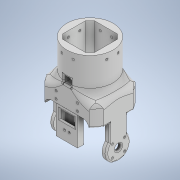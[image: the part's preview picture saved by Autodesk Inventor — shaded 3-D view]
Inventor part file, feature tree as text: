
AUTODESK INVENTOR PART (.ipt)
format: ipt  version: 2021 (Build 250183000, 183)  size: 1,526,272 bytes
history: native  units: mm
features: sketch x24, extrude x23, fillet x15, other x1
ambient origin geometry x8: Origin, YZ Plane, XZ Plane, XY Plane, X Axis, Y Axis, Z Axis, Center Point
bodies: Body1 (feature_tree)
feature tree (63):
  other  "Sólido1"
  extrude  "Extrusión1"  Depth=40.0mm
  extrude  "Extrusión2"  Depth=2.0mm
  fillet  "Empalme1"  Radius=400.0mm
  extrude  "Extrusión3"  Depth=40.0mm TaperAngle=0.0deg
  extrude  "Extrusión4"  Depth=12.0mm TaperAngle=0.0deg
  extrude  "Extrusión5"  Depth=9.0mm TaperAngle=0.0deg
  extrude  "Extrusión7"  Depth=2.0mm
  extrude  "Extrusión8"  Depth=50.0mm TaperAngle=0.0deg
  extrude  "Extrusión9"  Depth=10.0mm
  fillet  "Empalme2"  Radius=10.0mm
  fillet  "Empalme3"  Radius=10.0mm
  extrude  "Extrusión10"  Depth=10.0mm
  extrude  "Extrusión11"  Depth=10.0mm
  fillet  "Empalme4"  Radius=3.0mm
  fillet  "Empalme5"  Radius=500.0mm
  fillet  "Empalme6"  Radius=3.0mm
  fillet  "Empalme7"  Radius=3.0mm
  fillet  "Empalme8"  Radius=500.0mm
  fillet  "Empalme9"  Radius=3.0mm
  fillet  "Empalme10"  Radius=3.0mm
  extrude  "Extrusión12"  Depth=3.0mm
  extrude  "Extrusión13"  Depth=5.0mm
  extrude  "Extrusión14"  Depth=10.0mm
  extrude  "Extrusión15"  Depth=2.0mm
  fillet  "Empalme11"  Radius=0.1mm
  fillet  "Empalme12"  Radius=1.5mm
  extrude  "Extrusión16"  Depth=30.0mm TaperAngle=0.0deg
  extrude  "Extrusión17"  Depth=40.0mm TaperAngle=360.0deg
  extrude  "Extrusión18"  Depth=2.0mm
  fillet  "Empalme14"  Radius=18.0mm
  sketch  "Boceto25"  dims[d130=16.0mm d133=30.0mm d134=40.0mm d135=0.0mm]
  extrude  "Extrusión19"  Depth=30.0mm
  fillet  "Empalme15"  Radius=40.0mm
  extrude  "Extrusión20"  Depth=25.0mm TaperAngle=0.0deg
  extrude  "Extrusión22"  Depth=5.0mm TaperAngle=0.0deg
  extrude  "Extrusión23"  Depth=2.0mm
  extrude  "Extrusión24"  [1 undecoded]
  extrude  "Extrusión25"  [1 undecoded]
  fillet  "Empalme16"  [1 undecoded]
  sketch  "Boceto1"  dims[d7=40.0mm d8=0.0mm d10=8.0mm]
  sketch  "Boceto2"  dims[d11=400.0mm d12=0.0mm d13=2.0mm d16=400.0mm d17=0.0mm]
  sketch  "Boceto3"  dims[d18=400.0mm d19=0.0mm d20=40.0mm d21=0.0mm]
  sketch  "Boceto4"  dims[d25=62.249mm d26=0.0mm d27=12.0mm d28=0.0mm]
  sketch  "Boceto5"  dims[d32=9.0mm d37=160.0mm d38=0.0mm]
  sketch  "Boceto8"  dims[d39=2.0mm d40=2.0mm]
  sketch  "Boceto9"  dims[d47=160.0mm d48=0.0mm d49=50.0mm d50=0.0mm]
  sketch  "Boceto13"  dims[d51=10.0mm d52=10.0mm d53=10.0mm d54=10.0mm]
  sketch  "Boceto15"  dims[d55=10.0mm d56=10.0mm]
  sketch  "Boceto16"  dims[d57=10.0mm d62=3.0mm d63=3.0mm d64=500.0mm d65=0.0mm d70=3.0mm d71=3.0mm d72=500.0mm d73=0.0mm d79=3.0mm d80=3.0mm]
  sketch  "Boceto17"  dims[d81=3.0mm d82=3.0mm]
  sketch  "Boceto18"  dims[d83=15.0mm d84=0.0mm d87=5.0mm]
  sketch  "Boceto20"  dims[d88=10.0mm d90=10.0mm]
  sketch  "Boceto21"  dims[d91=15.0mm d92=0.0mm d93=2.0mm d94=0.1mm d95=1.5mm d96=0.0mm]
  sketch  "Boceto22"  dims[d106=100.0mm d107=0.0mm d109=30.0mm d110=0.0mm]
  sketch  "Boceto23"  dims[d111=2.0mm d114=40.0mm d116=360.0deg]
  sketch  "Boceto24"  dims[d118=1000.0mm d119=0.0mm d120=2.0mm d121=18.0mm d122=0.0mm]
  sketch  "Boceto26"  dims[d142=35.0mm d143=0.0mm d150=25.0mm d151=0.0mm]
  sketch  "Boceto27"  dims[d153=10.0mm d154=5.0mm d155=0.0mm]
  sketch  "Boceto30"  dims[d156=2.0mm d108=0.5mm]
  sketch  "Boceto31"
  sketch  "Boceto32"
  sketch  "Boceto33"
note: 3 required parameter values undecoded (feature->parameter linkage not recoverable at this tier; creation-order binding heuristic only, values carry confidence <= 0.55)
